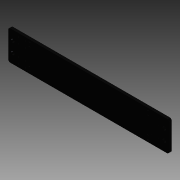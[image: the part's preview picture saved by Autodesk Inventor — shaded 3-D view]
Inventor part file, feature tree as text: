
AUTODESK INVENTOR PART (.ipt)
format: ipt  version: 2013 (Build 170138000, 138)  size: 177,152 bytes
history: native  units: in
note: dims shown in document units (in); Inventor stores cm internally (conversion verified against a paired STEP export)
features: reference x2, extrude x1, sketch x1
ambient origin geometry x8: Origin, YZ Plane, XZ Plane, XY Plane, X Axis, Y Axis, Z Axis, Center Point
bodies: Solid1 (feature_tree)
feature tree (4):
  extrude  "Extrusion1"  [1 undecoded]
  sketch  "Sketch1"  dims[d0=0.255in d1=0.0in]
  reference  "Reference1"
  reference  "Reference2"
note: 1 required parameter value undecoded (feature->parameter linkage not recoverable at this tier; creation-order binding heuristic only, values carry confidence <= 0.55)
